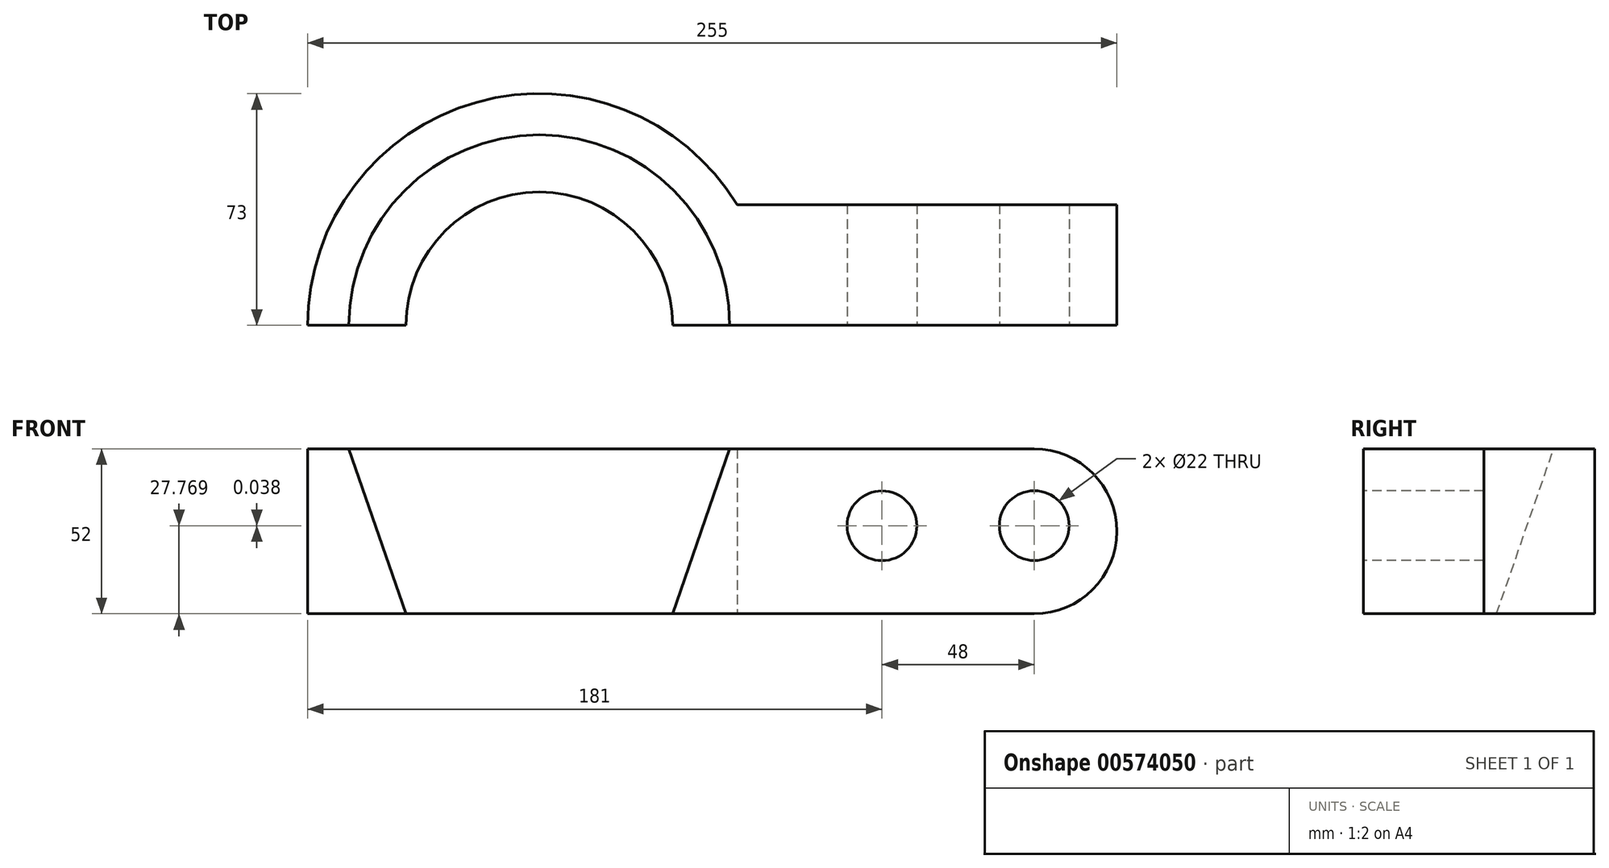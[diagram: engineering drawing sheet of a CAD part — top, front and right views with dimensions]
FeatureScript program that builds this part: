
annotation { "Feature Type Name" : "Feature", "Feature Type Description" : "" }
export const myFeature = defineFeature(function(context is Context, id is Id, definition is map)
    precondition{}
    {
        {
            var Q0;
            Q0=qCreatedBy(makeId("Top.planeOp"),FACE);
            var sketch = newSketch(context, id + "F0", { "sketchPlane" : qUnion([Q0])});
            skArc(sketch, "E0", {"start": v(42, 0) * mm, "mid": v(0, 42) * mm, "end": v(-42, 0) * mm});
            skArc(sketch, "E1", {"start": v(62.33, 38) * mm, "mid": v(-19.73, 70.28) * mm, "end": v(-73, 0) * mm});
            skLineSegment(sketch, "E2", {"start": v(-73, 0) * mm, "end": v(-42, 0) * mm});
            skLineSegment(sketch, "E3.trimOffspring", {"start": v(42, 0) * mm, "end": v(73, 0) * mm});
            skLineSegment(sketch, "E4", {"start": v(62.33, 38) * mm, "end": v(182, 38) * mm});
            skLineSegment(sketch, "E5", {"start": v(182, 38) * mm, "end": v(182, 0) * mm});
            skLineSegment(sketch, "E6", {"start": v(182, 0) * mm, "end": v(73, 0) * mm});
            skSolve(sketch);
        }
        {
            var Q0;
            Q0=makeQuery(id+"F0.imprint","IMPRINT",FACE,{"disambiguationData":[TD([[makeQuery(id+"F0.imprint","IMPRINT",EDGE,{"derivedFrom":sQuery(id+"F0.wireOp",EDGE,"E0")}),-1.0]])]});
            extrude(context, id + "F1", {"entities" : qUnion([Q0]), "depth" : 52 * mm, "offsetDistance" : 25 * mm});
        }
        {
            var Q0;
            Q0=makeQuery(id+"F1.opExtrude","SWEPT_FACE",FACE,{"disambiguationData":[OSD([sQuery(id+"F0.wireOp",EDGE,"E2")])]});
            var sketch = newSketch(context, id + "F2", { "sketchPlane" : qUnion([Q0])});
            skLineSegment(sketch, "E7", {"start": v(-60, 52) * mm, "end": v(-42, 0) * mm});
            skLineSegment(sketch, "E8", {"start": v(-42, 0) * mm, "end": v(-42, 52) * mm});
            skLineSegment(sketch, "E9", {"start": v(-42, 52) * mm, "end": v(-60, 52) * mm});
            skLineSegment(sketch, "E10", {"start": v(0, 51.93) * mm, "end": v(0, 0) * mm});
            skSolve(sketch);
        }
        {
            var Q0;
            Q0 = qSketchRegion(id + "F2", true);
            var Q1;
            Q1=sQuery(id+"F2.wireOp",EDGE,"E10");
            revolve(context, id + "F3", {"operationType" : NewBodyOperationType.REMOVE, "entities" : qUnion([Q0]), "axis" : qUnion([Q1]), "revolveType" : RevolveType.FULL});
        }
        {
            var Q0;
            Q0=makeQuery(id+"F1.opExtrude","SWEPT_FACE",FACE,{"disambiguationData":[OSD([sQuery(id+"F0.wireOp",EDGE,"E3.trimOffspring"),sQuery(id+"F0.wireOp",EDGE,"E6")])]});
            var sketch = newSketch(context, id + "F4", { "sketchPlane" : qUnion([Q0])});
            skCircle(sketch, "E11", {"center": v(108, 27.77) * mm, "radius": 11 * mm});
            skCircle(sketch, "E12", {"center": v(156, 27.8) * mm, "radius": 11 * mm});
            skSolve(sketch);
        }
        {
            var Q0;
            Q0=makeQuery(id+"F4.imprint","IMPRINT",FACE,{"disambiguationData":[TD([[makeQuery(id+"F4.imprint","IMPRINT",EDGE,{"derivedFrom":sQuery(id+"F4.wireOp",EDGE,"E11")}),1.0]])]});
            var Q1;
            Q1=makeQuery(id+"F4.imprint","IMPRINT",FACE,{"disambiguationData":[TD([[makeQuery(id+"F4.imprint","IMPRINT",EDGE,{"derivedFrom":sQuery(id+"F4.wireOp",EDGE,"E12")}),1.0]])]});
            extrude(context, id + "F5", {"entities" : qUnion([Q0, Q1]), "operationType" : NewBodyOperationType.REMOVE, "oppositeDirection" : true, "depth" : 154 * mm, "offsetDistance" : 25 * mm});
        }
        {
            var Q0;
            Q0=makeQuery(id+"F1.opExtrude","CAP_EDGE",EDGE,{"disambiguationData":[OSD([sQuery(id+"F0.wireOp",EDGE,"E5")])],"isStart":false});
            var Q1;
            Q1=makeQuery(id+"F1.opExtrude","CAP_EDGE",EDGE,{"disambiguationData":[OSD([sQuery(id+"F0.wireOp",EDGE,"E5")])],"isStart":true});
            fillet(context, id + "F6", {"entities" : qUnion([Q0, Q1]), "radius" : 26 * mm, "tangentPropagation" : true, "allowEdgeOverflow" : false});
        }
    });
